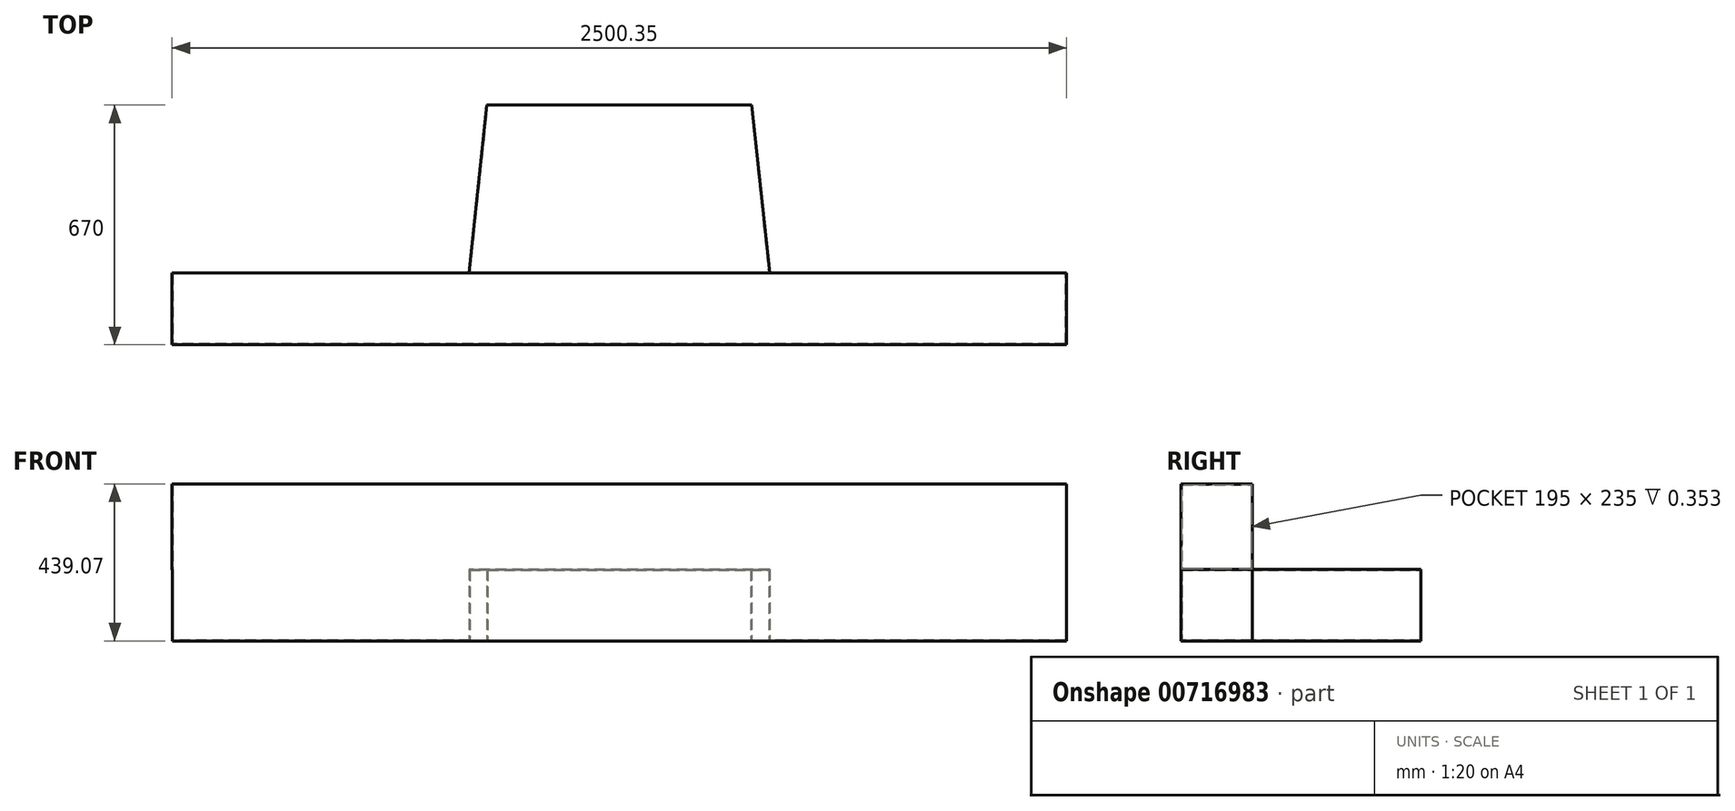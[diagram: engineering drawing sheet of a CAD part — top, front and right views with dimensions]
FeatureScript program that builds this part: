
annotation { "Feature Type Name" : "Feature", "Feature Type Description" : "" }
export const myFeature = defineFeature(function(context is Context, id is Id, definition is map)
    precondition{}
    {
        {
            var Q0;
            Q0=qCreatedBy(makeId("Top.planeOp"),FACE);
            var sketch = newSketch(context, id + "F0", { "sketchPlane" : qUnion([Q0])});
            skLineSegment(sketch, "E0", {"start": v(-205.65, 0) * mm, "end": v(2294.35, 0) * mm});
            skLineSegment(sketch, "E1", {"start": v(2294.35, 0) * mm, "end": v(2294.35, 200) * mm});
            skLineSegment(sketch, "E2", {"start": v(2294.35, 200) * mm, "end": v(-205.65, 200) * mm});
            skLineSegment(sketch, "E3", {"start": v(-205.65, 200) * mm, "end": v(-205.65, 0) * mm});
            skLineSegment(sketch, "E4", {"start": v(624.35, 200) * mm, "end": v(674.35, 670) * mm});
            skLineSegment(sketch, "E5", {"start": v(674.35, 670) * mm, "end": v(1414.35, 670) * mm});
            skLineSegment(sketch, "E6", {"start": v(1414.35, 670) * mm, "end": v(1464.35, 200) * mm});
            skLineSegment(sketch, "E7", {"start": v(-205.65, 200) * mm, "end": v(624.35, 200) * mm});
            skLineSegment(sketch, "E8", {"start": v(1464.35, 200) * mm, "end": v(2294.35, 200) * mm});
            skLineSegment(sketch, "E9", {"start": v(1044.35, 670) * mm, "end": v(1044.35, 200) * mm});
            skSolve(sketch);
        }
        {
            var Q0;
            Q0 = qSketchRegion(id + "F0", true);
            extrude(context, id + "F1", {"entities" : qUnion([Q0]), "depth" : 200 * mm, "offsetDistance" : 25 * mm});
        }
        {
            var Q0;
            Q0=qCreatedBy(makeId("Right.planeOp"),FACE);
            var sketch = newSketch(context, id + "F2", { "sketchPlane" : qUnion([Q0])});
            skLineSegment(sketch, "E10.bottom", {"start": v(0, 199.07) * mm, "end": v(200, 199.07) * mm});
            skLineSegment(sketch, "E10.top", {"start": v(0, 439.07) * mm, "end": v(200, 439.07) * mm});
            skLineSegment(sketch, "E10.left", {"start": v(0, 439.07) * mm, "end": v(0, 199.07) * mm});
            skLineSegment(sketch, "E10.right", {"start": v(200, 439.07) * mm, "end": v(200, 199.07) * mm});
            skSolve(sketch);
        }
        {
            var Q0;
            Q0=makeQuery(id+"F2.imprint","IMPRINT",FACE,{"disambiguationData":[TD([[makeQuery(id+"F2.imprint","IMPRINT",EDGE,{"derivedFrom":sQuery(id+"F2.wireOp",EDGE,"E10.bottom")}),1.0]])]});
            extrude(context, id + "F3", {"entities" : qUnion([Q0]), "operationType" : NewBodyOperationType.ADD, "depth" : 2294 * mm, "offsetDistance" : 25 * mm, "hasSecondDirection" : true, "secondDirectionOppositeDirection" : true, "secondDirectionDepth" : 206 * mm});
        }
        {
            var Q0;
            Q0=makeQuery(id+"F1.opExtrude","SWEPT_FACE",FACE,{"disambiguationData":[OSD([sQuery(id+"F0.wireOp",EDGE,"E5")])]});
            shell(context, id + "F4", {"entities" : qUnion([Q0]), "thickness" : 2.5 * mm});
        }
    });
